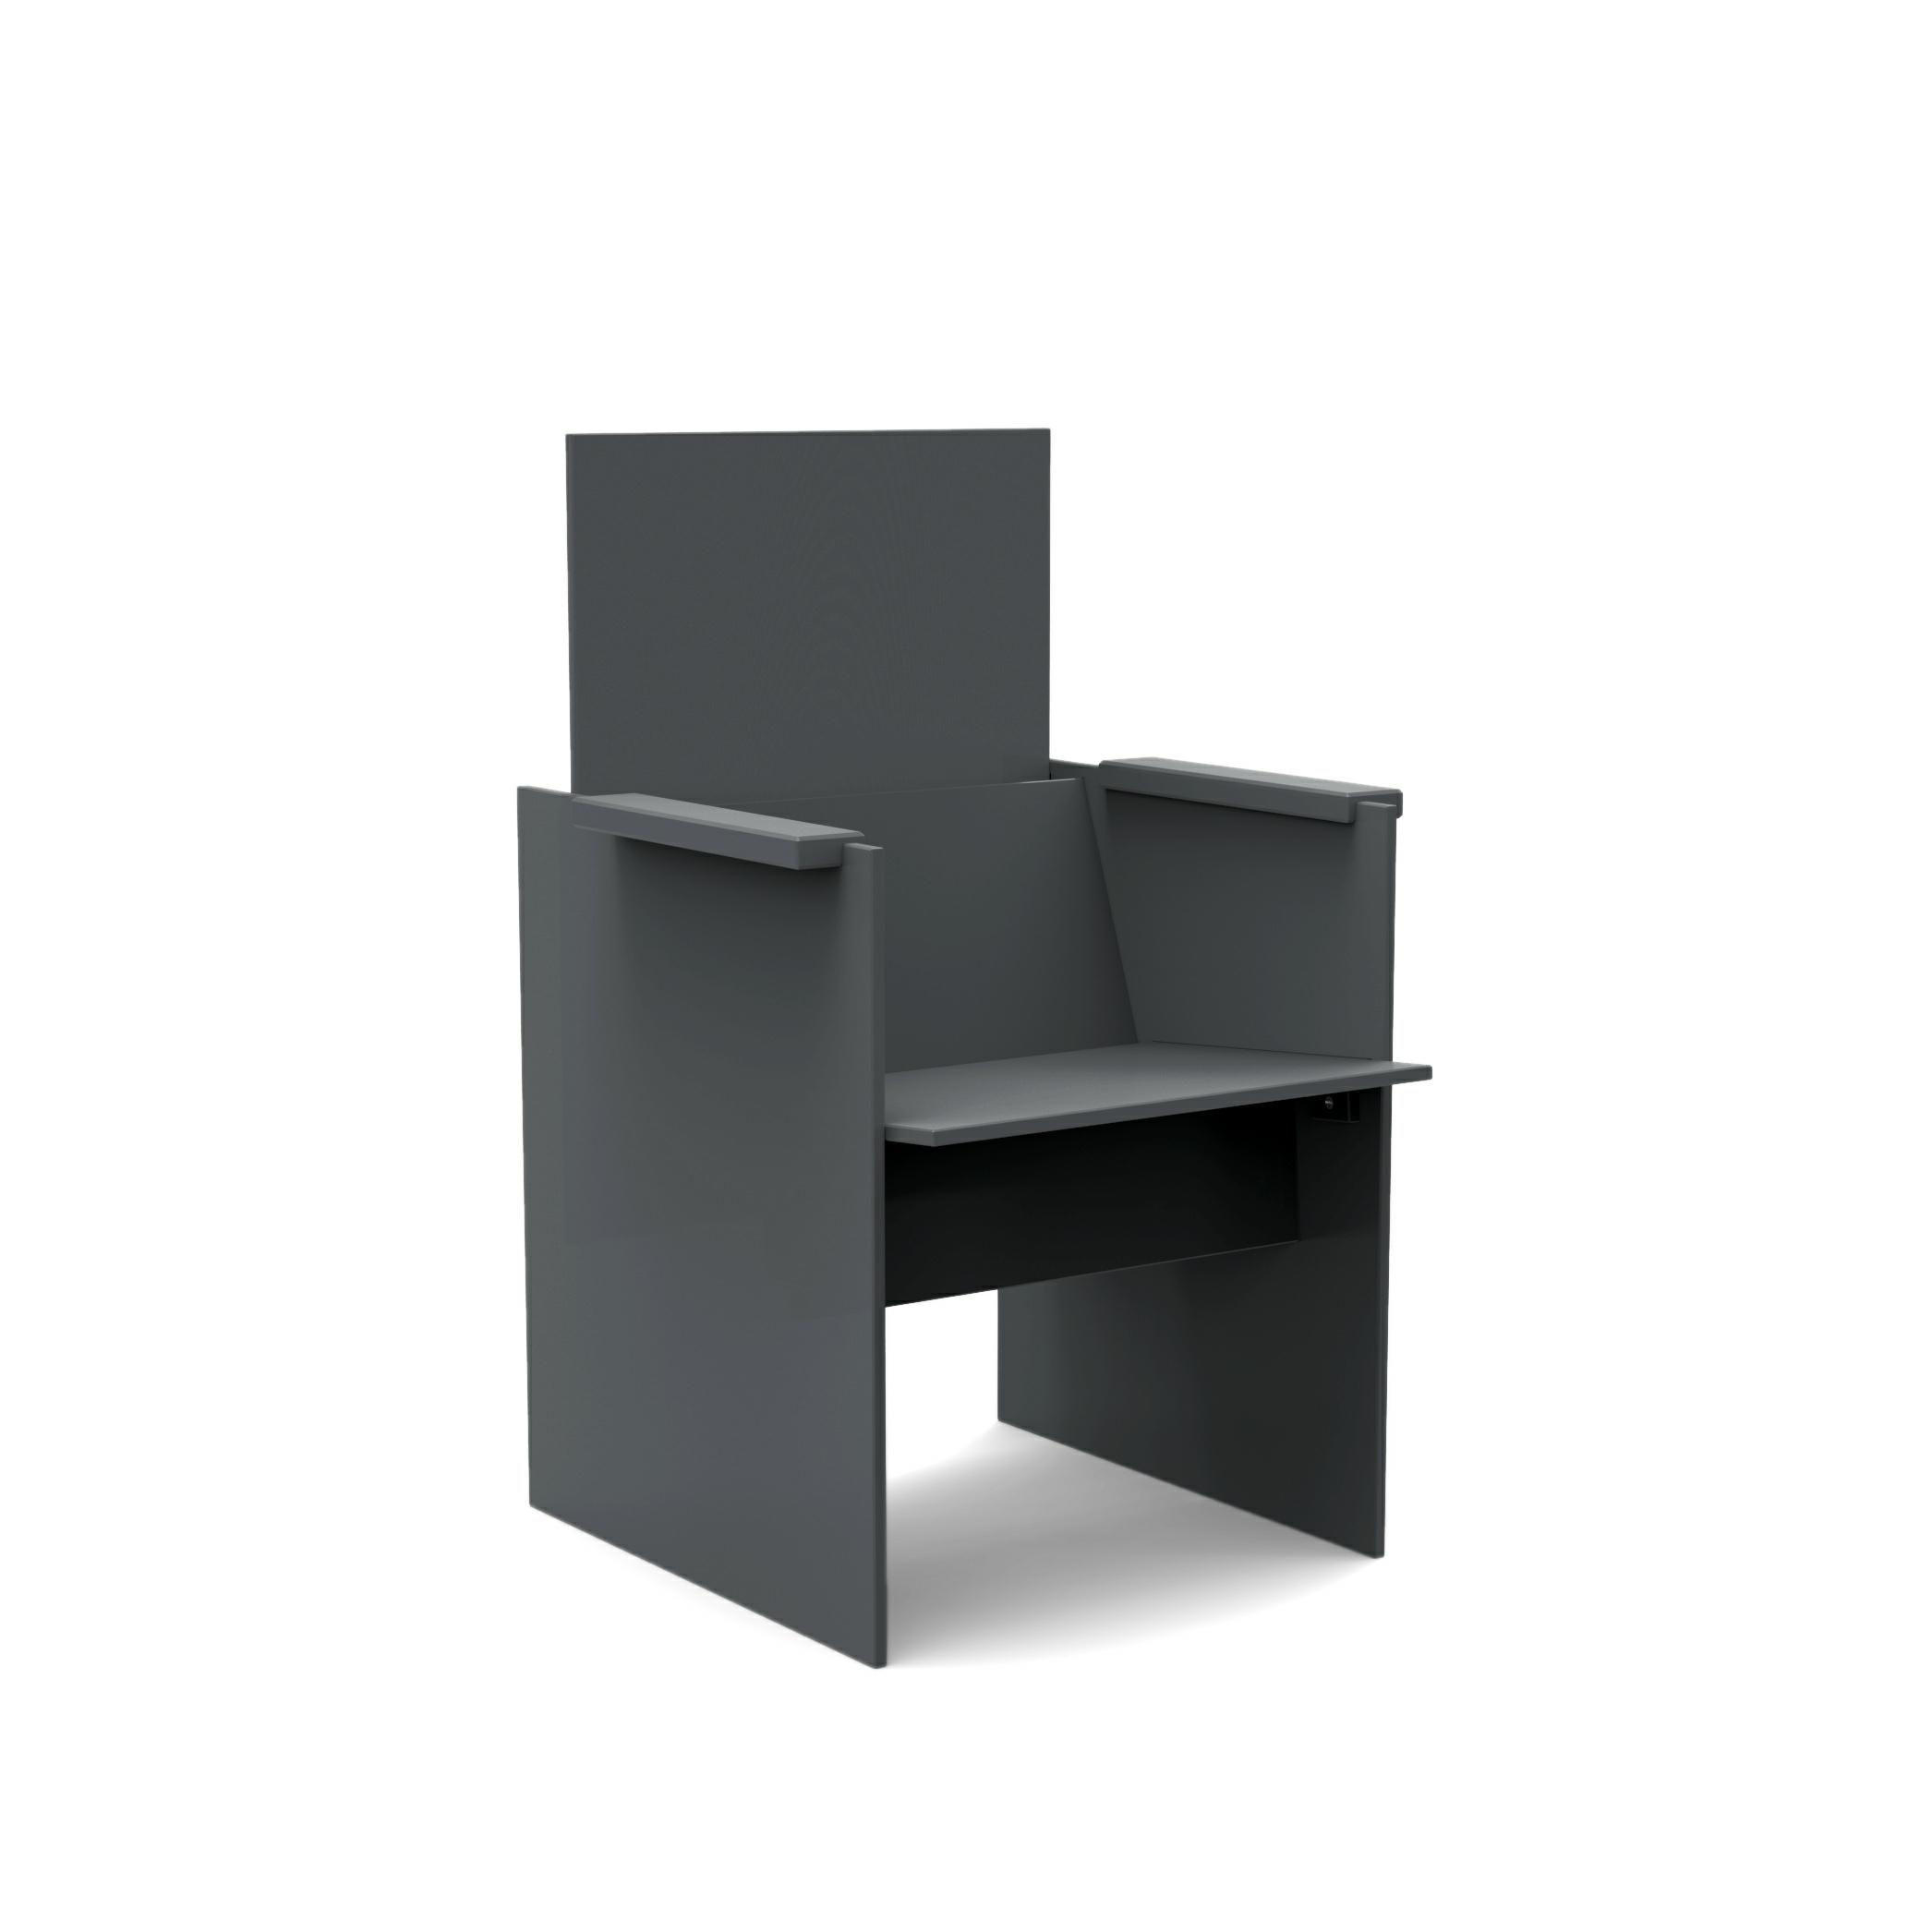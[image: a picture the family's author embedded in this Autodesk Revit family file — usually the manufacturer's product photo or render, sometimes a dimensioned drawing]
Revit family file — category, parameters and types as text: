
# Revit family: Lollygagger Salmela Lussi
name_source: partatom
category: Furniture
revit_build: Autodesk Revit 2016 (Build: 20150220_1215(x64)
units: mm (PartAtom-declared; Revit-internal decimal feet)

## family parameters
Always vertical = Yes
Cut with Voids When Loaded = No
OmniClass Number = 23.40.20.00
OmniClass Title = General Furniture and Specialties
Room Calculation Point = No
Shared = No
Work Plane-Based = No

## types (10) — shared parameters
Height = 37 1/2"
Length = 24"
Manufacturer = Loll
Thick = 1/2"
Type Image = Salmela Lussi.jpg
URL = https://lolldesigns.com
Width = 24 17/32"

## per-type parameters (varying)
| type | Finish Material |
| Loll-Black | Loll-Leaf |
| Loll-Sunset | Loll-Sunset |
| Loll-Chocolate | Loll-Chocolate |
| Loll-Sky | Loll-Sky |
| Loll-Apple | Loll-Apple |
| Loll-Leaf | Loll-Leaf |
| Loll-Charcoal | Loll-Charcoal |
| Loll-Navy Blue | Loll-Navy Blue |
| Loll-White | Loll-White |
| Loll-Driftwood | Loll-Driftwood |

## geometry (parser evidence)
native form markers: Sweep x3
no freeform markers — native parametric forms only
